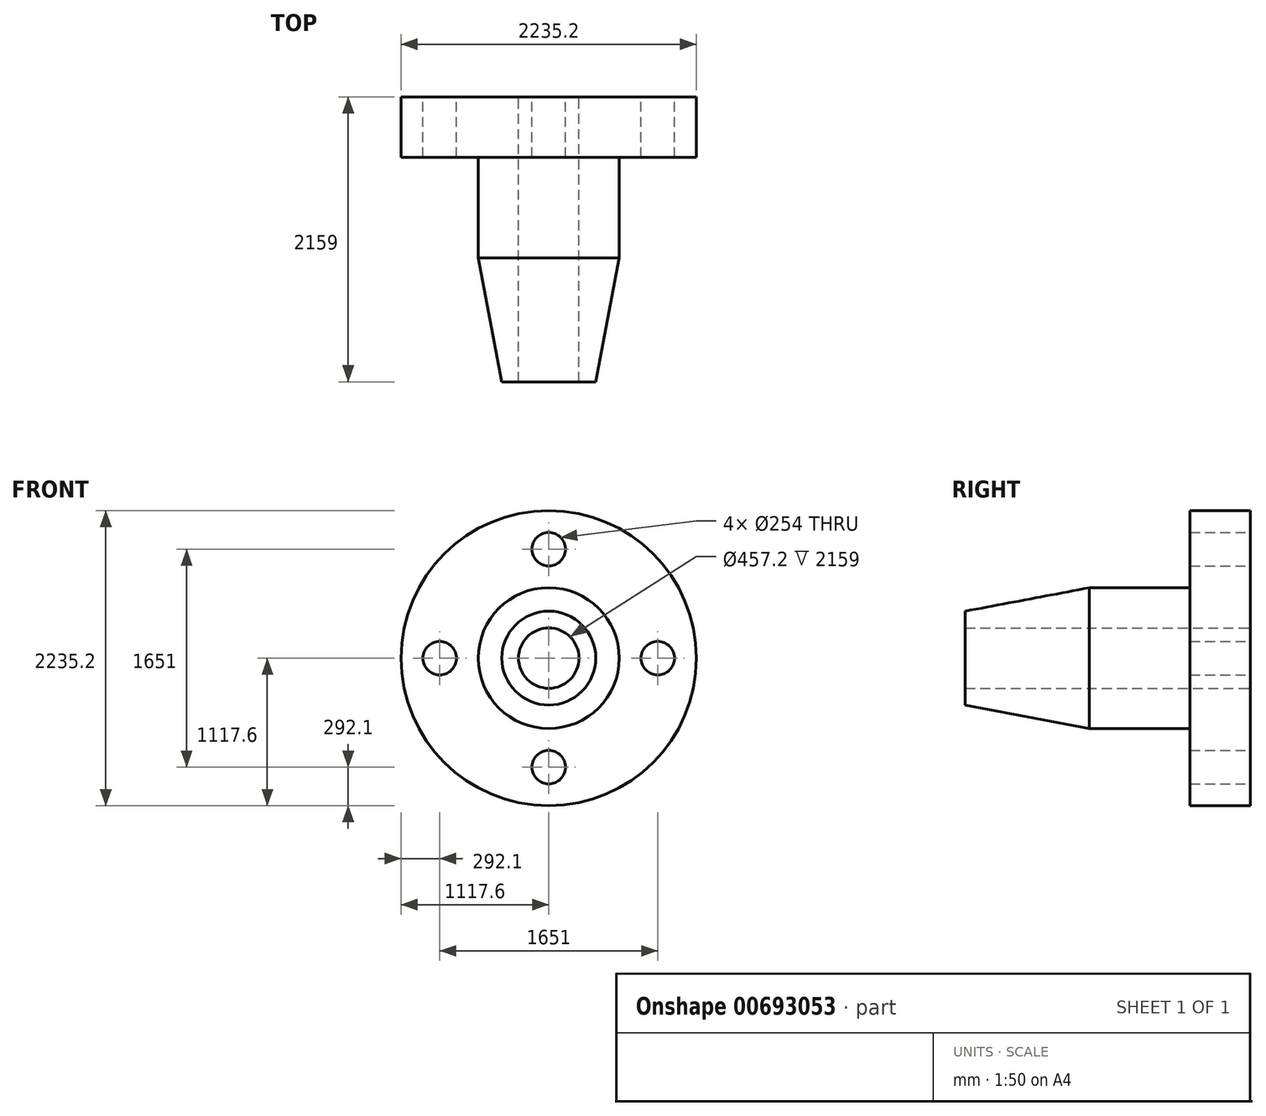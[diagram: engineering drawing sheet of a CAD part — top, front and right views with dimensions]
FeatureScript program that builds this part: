
annotation { "Feature Type Name" : "Feature", "Feature Type Description" : "" }
export const myFeature = defineFeature(function(context is Context, id is Id, definition is map)
    precondition{}
    {
        {
            var Q0;
            Q0=qCreatedBy(makeId("Top.planeOp"),FACE);
            var sketch = newSketch(context, id + "F0", { "sketchPlane" : qUnion([Q0])});
            skLineSegment(sketch, "E0", {"start": v(0, 0) * mm, "end": v(0, -2159) * mm, "construction": true});
            skPoint(sketch, "E1", {"position": v(228.6, 0) * mm});
            skPoint(sketch, "E2", {"position": v(228.6, -2159) * mm});
            skLineSegment(sketch, "E3", {"start": v(228.6, 0) * mm, "end": v(228.6, -2159) * mm});
            skPoint(sketch, "E4", {"position": v(355.6, -2159) * mm});
            skLineSegment(sketch, "E5", {"start": v(228.6, -2159) * mm, "end": v(355.6, -2159) * mm});
            skLineSegment(sketch, "E6", {"start": v(228.6, 0) * mm, "end": v(1117.6, 0) * mm});
            skLineSegment(sketch, "E7", {"start": v(1117.6, 0) * mm, "end": v(1117.6, -457.2) * mm});
            skPoint(sketch, "E8", {"position": v(533.4, -2159) * mm});
            skPoint(sketch, "E9", {"position": v(533.4, -1219.2) * mm});
            skPoint(sketch, "E10", {"position": v(533.4, -457.2) * mm});
            skLineSegment(sketch, "E11", {"start": v(533.4, -457.2) * mm, "end": v(533.4, -1219.2) * mm});
            skLineSegment(sketch, "E12", {"start": v(533.4, -457.2) * mm, "end": v(1117.6, -457.2) * mm});
            skLineSegment(sketch, "E13", {"start": v(533.4, -1219.2) * mm, "end": v(355.6, -2159) * mm});
            skSolve(sketch);
        }
        {
            var Q0;
            Q0=makeQuery(id+"F0.imprint","IMPRINT",FACE,{"disambiguationData":[TD([[makeQuery(id+"F0.imprint","IMPRINT",EDGE,{"derivedFrom":sQuery(id+"F0.wireOp",EDGE,"E3")}),1.0]])]});
            var sketch = newSketch(context, id + "F1", { "sketchPlane" : qUnion([Q0])});
            skSolve(sketch);
        }
        {
            var Q0;
            Q0=makeQuery(id+"F1.imprint","IMPRINT",FACE,{"disambiguationData":[TD([[makeQuery(id+"F1.imprint","IMPRINT",EDGE,{"derivedFrom":makeQuery(id+"F0.imprint","IMPRINT",EDGE,{"derivedFrom":sQuery(id+"F0.wireOp",EDGE,"E3")})}),1.0]])]});
            var Q1;
            Q1=sQuery(id+"F0.wireOp",EDGE,"E0");
            revolve(context, id + "F2", {"entities" : qUnion([Q0]), "axis" : qUnion([Q1]), "revolveType" : RevolveType.FULL});
        }
        {
            var Q0;
            Q0=makeQuery(id+"F2.opRevolve","SWEPT_FACE",FACE,{"disambiguationData":[OSD([sQuery(id+"F0.wireOp",EDGE,"E6")])]});
            var sketch = newSketch(context, id + "F3", { "sketchPlane" : qUnion([Q0])});
            skPoint(sketch, "E14", {"position": v(0, 228.6) * mm});
            skPoint(sketch, "E15", {"position": v(0, 1117.6) * mm});
            skPoint(sketch, "E16", {"position": v(-228.6, 0) * mm});
            skPoint(sketch, "E17", {"position": v(-1117.6, 0) * mm});
            skPoint(sketch, "E18", {"position": v(0, -228.6) * mm});
            skPoint(sketch, "E19", {"position": v(0, -1117.6) * mm});
            skPoint(sketch, "E20", {"position": v(228.6, 0) * mm});
            skPoint(sketch, "E21", {"position": v(1117.6, 0) * mm});
            skPoint(sketch, "E22", {"position": v(0, 825.5) * mm});
            skPoint(sketch, "E23", {"position": v(-825.5, 0) * mm});
            skPoint(sketch, "E24", {"position": v(0, -825.5) * mm});
            skPoint(sketch, "E25", {"position": v(825.5, 0) * mm});
            skCircle(sketch, "E26", {"center": v(0, 825.5) * mm, "radius": 127 * mm});
            skCircle(sketch, "E27", {"center": v(825.5, 0) * mm, "radius": 127 * mm});
            skCircle(sketch, "E28", {"center": v(0, -825.5) * mm, "radius": 127 * mm});
            skCircle(sketch, "E29", {"center": v(-825.5, 0) * mm, "radius": 127 * mm});
            skSolve(sketch);
        }
        {
            var Q0;
            Q0=sQuery(id+"F3.wireOp",VERTEX,"E26.center");
            var Q1;
            Q1=sQuery(id+"F3.wireOp",VERTEX,"E23");
            var Q2;
            Q2=sQuery(id+"F3.wireOp",VERTEX,"E25");
            var Q3;
            Q3=sQuery(id+"F3.wireOp",VERTEX,"E24");
            var Q4;
            Q4=makeQuery(id+"F2.opRevolve","SWEPT_BODY",BODY,{"disambiguationData":[OSD([sQuery(id+"F0.wireOp",EDGE,"E3"),sQuery(id+"F0.wireOp",EDGE,"E5"),sQuery(id+"F0.wireOp",EDGE,"E6"),sQuery(id+"F0.wireOp",EDGE,"E7"),sQuery(id+"F0.wireOp",EDGE,"E11"),sQuery(id+"F0.wireOp",EDGE,"E12"),sQuery(id+"F0.wireOp",EDGE,"E13")])]});
            hole(context, id + "F4", {"style" : HoleStyle.SIMPLE, "endStyle" : HoleEndStyle.THROUGH, "holeDiameter" : 254 * mm, "majorDiameter" : 6.35 * mm, "isTappedThrough" : true, "tappedDepth" : 12.7 * mm, "tapClearance" : 3, "locations" : qUnion([Q0, Q1, Q2, Q3]), "scope" : qUnion([Q4])});
        }
    });
